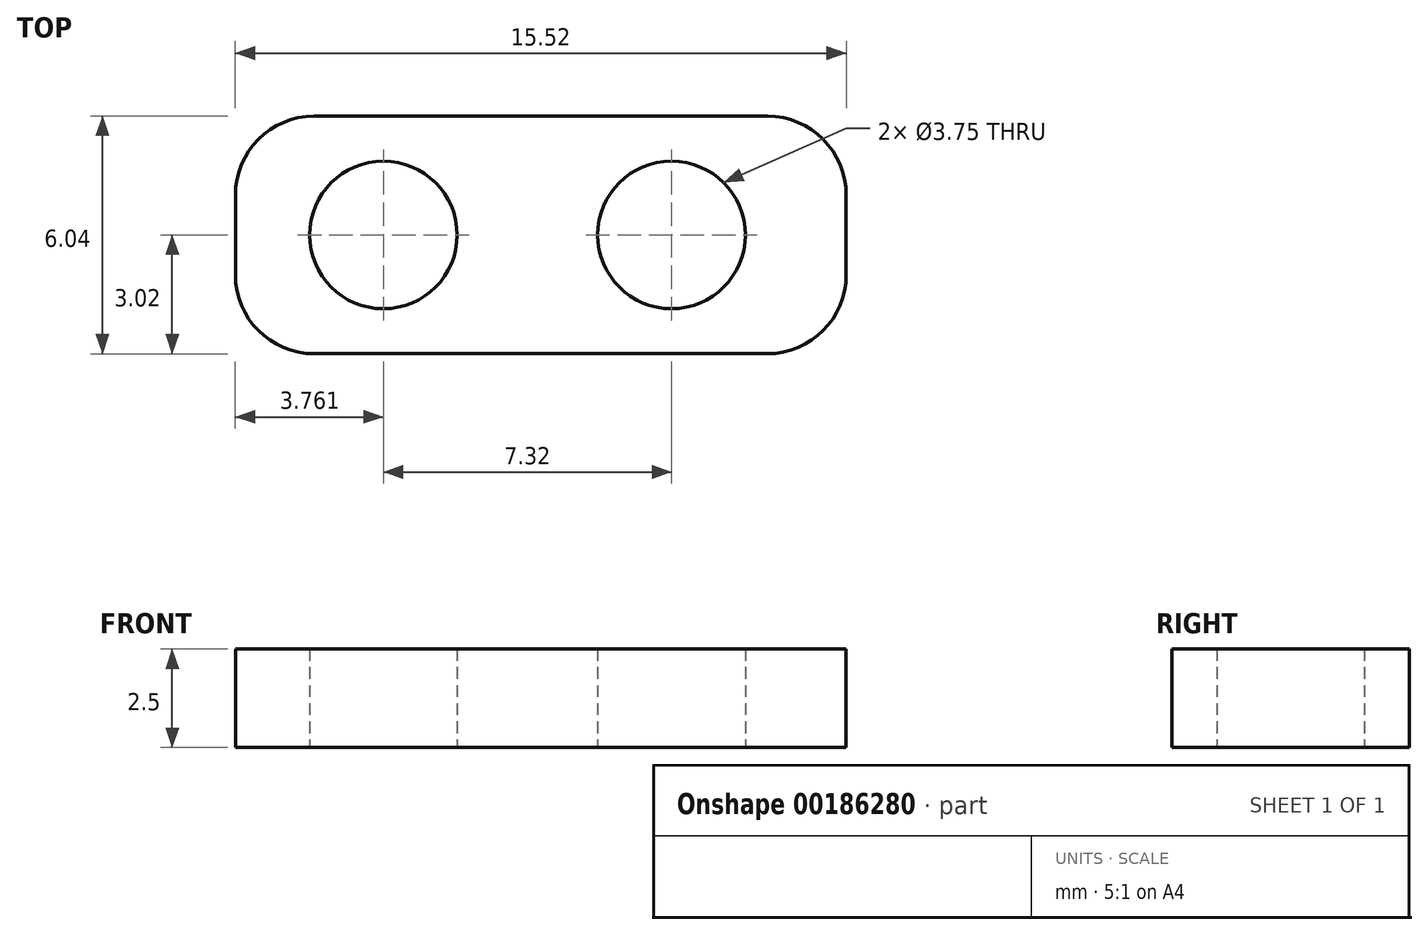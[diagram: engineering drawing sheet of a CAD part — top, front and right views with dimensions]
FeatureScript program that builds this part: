
annotation { "Feature Type Name" : "Feature", "Feature Type Description" : "" }
export const myFeature = defineFeature(function(context is Context, id is Id, definition is map)
    precondition{}
    {
        {
            var Q0;
            Q0=qCreatedBy(makeId("Top.planeOp"),FACE);
            var sketch = newSketch(context, id + "F0", { "sketchPlane" : qUnion([Q0])});
            skPoint(sketch, "E0", {"position": v(3.32, 0) * mm});
            skPoint(sketch, "E1", {"position": v(-4, 0) * mm});
            skCircle(sketch, "E2", {"center": v(3.32, 0) * mm, "radius": 1.88 * mm});
            skCircle(sketch, "E3", {"center": v(-4, 0) * mm, "radius": 1.88 * mm});
            skLineSegment(sketch, "E4.bottom", {"start": v(7.76, -3.02) * mm, "end": v(-7.76, -3.02) * mm});
            skLineSegment(sketch, "E4.top", {"start": v(7.76, 3.02) * mm, "end": v(-7.76, 3.02) * mm});
            skLineSegment(sketch, "E4.left", {"start": v(7.76, -3.02) * mm, "end": v(7.76, 3.02) * mm});
            skLineSegment(sketch, "E4.right", {"start": v(-7.76, -3.02) * mm, "end": v(-7.76, 3.02) * mm});
            skPoint(sketch, "E4.middle", {"position": v(0, 0) * mm});
            skSolve(sketch);
        }
        {
            var Q0;
            Q0=makeQuery(id+"F0.imprint","IMPRINT",FACE,{"disambiguationData":[TD([[makeQuery(id+"F0.imprint","IMPRINT",EDGE,{"derivedFrom":sQuery(id+"F0.wireOp",EDGE,"E2")}),-1.0]])]});
            extrude(context, id + "F1", {"entities" : qUnion([Q0]), "depth" : 2.5 * mm, "offsetDistance" : 25 * mm});
        }
        {
            var Q0;
            Q0=makeQuery(id+"F1.opExtrude","SWEPT_EDGE",EDGE,{"disambiguationData":[OSD([sQuery(id+"F0.wireOp",EDGE,"E4.top"),sQuery(id+"F0.wireOp",EDGE,"E4.left")])]});
            var Q1;
            Q1=makeQuery(id+"F1.opExtrude","SWEPT_EDGE",EDGE,{"disambiguationData":[OSD([sQuery(id+"F0.wireOp",EDGE,"E4.bottom"),sQuery(id+"F0.wireOp",EDGE,"E4.left")])]});
            var Q2;
            Q2=makeQuery(id+"F1.opExtrude","SWEPT_EDGE",EDGE,{"disambiguationData":[OSD([sQuery(id+"F0.wireOp",EDGE,"E4.top"),sQuery(id+"F0.wireOp",EDGE,"E4.right")])]});
            var Q3;
            Q3=makeQuery(id+"F1.opExtrude","SWEPT_EDGE",EDGE,{"disambiguationData":[OSD([sQuery(id+"F0.wireOp",EDGE,"E4.bottom"),sQuery(id+"F0.wireOp",EDGE,"E4.right")])]});
            fillet(context, id + "F2", {"entities" : qUnion([Q0, Q1, Q2, Q3]), "tangentPropagation" : true, "radius" : 2 * mm, "defaultsChanged" : false, "vertexSettings" : [], "allowEdgeOverflow" : false});
        }
    });
